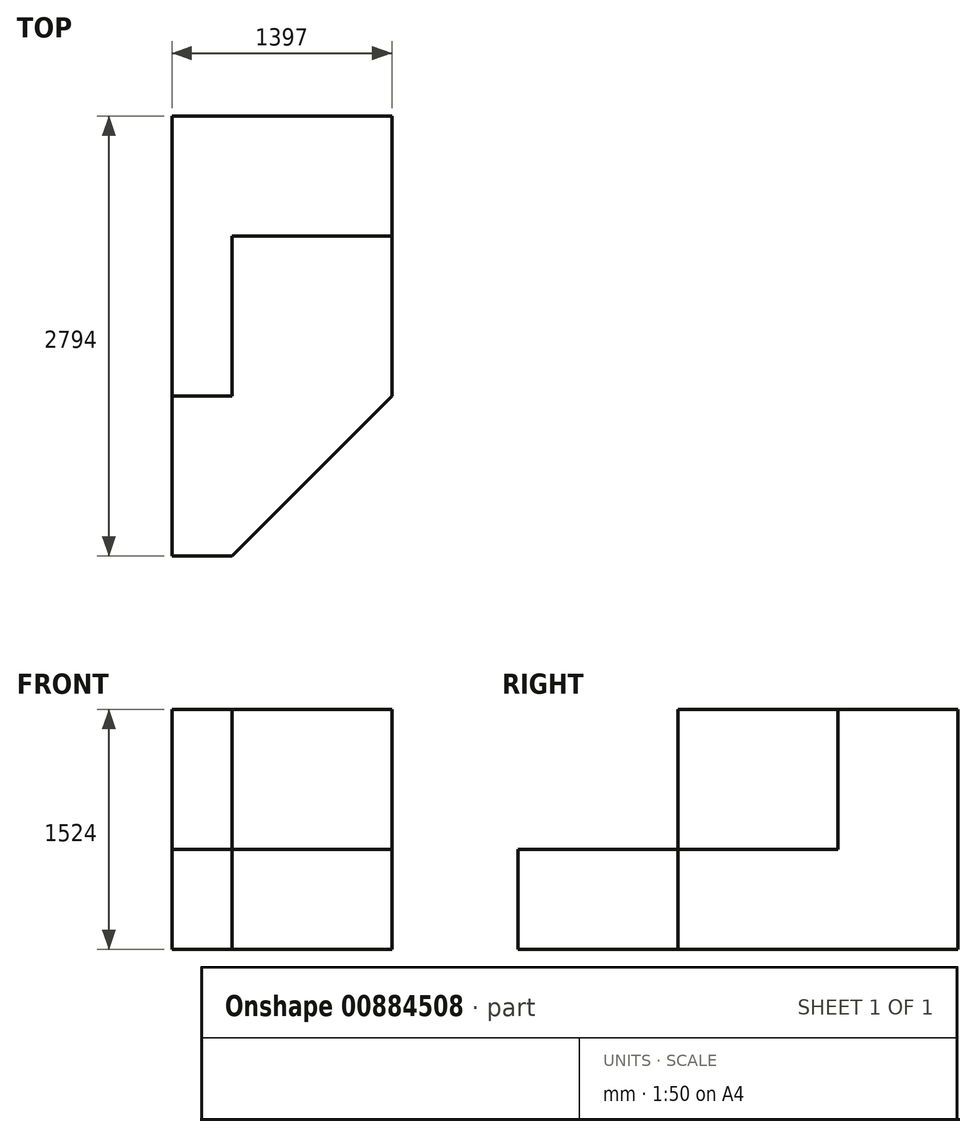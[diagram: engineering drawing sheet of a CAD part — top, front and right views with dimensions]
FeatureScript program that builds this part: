
annotation { "Feature Type Name" : "Feature", "Feature Type Description" : "" }
export const myFeature = defineFeature(function(context is Context, id is Id, definition is map)
    precondition{}
    {
        {
            var Q0;
            Q0=qCreatedBy(makeId("Top.planeOp"),FACE);
            var sketch = newSketch(context, id + "F0", { "sketchPlane" : qUnion([Q0])});
            skLineSegment(sketch, "E0.bottom", {"start": v(-1340.32, 2749.23) * mm, "end": v(56.68, 2749.23) * mm});
            skLineSegment(sketch, "E0.top", {"start": v(-1340.32, -44.77) * mm, "end": v(56.68, -44.77) * mm});
            skLineSegment(sketch, "E0.left", {"start": v(-1340.32, 2749.23) * mm, "end": v(-1340.32, -44.77) * mm});
            skLineSegment(sketch, "E0.right", {"start": v(56.68, 2749.23) * mm, "end": v(56.68, -44.77) * mm});
            skSolve(sketch);
        }
        {
            var Q0;
            Q0=makeQuery(id+"F0.imprint","IMPRINT",FACE,{"disambiguationData":[TD([[makeQuery(id+"F0.imprint","IMPRINT",EDGE,{"derivedFrom":sQuery(id+"F0.wireOp",EDGE,"E0.bottom")}),-1.0]])]});
            extrude(context, id + "F1", {"entities" : qUnion([Q0]), "depth" : 635 * mm, "offsetDistance" : 25.4 * mm});
        }
        {
            var Q0;
            Q0=makeQuery(id+"F1.opExtrude","CAP_FACE",FACE,{"disambiguationData":[OSD([sQuery(id+"F0.wireOp",EDGE,"E0.bottom"),sQuery(id+"F0.wireOp",EDGE,"E0.top"),sQuery(id+"F0.wireOp",EDGE,"E0.left"),sQuery(id+"F0.wireOp",EDGE,"E0.right")])],"isStart":false});
            var sketch = newSketch(context, id + "F2", { "sketchPlane" : qUnion([Q0])});
            skLineSegment(sketch, "E1", {"start": v(56.68, -44.77) * mm, "end": v(-959.32, -44.77) * mm});
            skLineSegment(sketch, "E2", {"start": v(56.68, -44.77) * mm, "end": v(56.68, 971.23) * mm});
            skLineSegment(sketch, "E3", {"start": v(56.68, 971.23) * mm, "end": v(-959.32, -44.77) * mm});
            skSolve(sketch);
        }
        {
            var Q0;
            Q0=makeQuery(id+"F2.imprint","IMPRINT",FACE,{"disambiguationData":[TD([[makeQuery(id+"F2.imprint","IMPRINT",EDGE,{"derivedFrom":sQuery(id+"F2.wireOp",EDGE,"E1")}),1.0]])]});
            extrude(context, id + "F3", {"entities" : qUnion([Q0]), "operationType" : NewBodyOperationType.REMOVE, "oppositeDirection" : true, "depth" : 660.4 * mm, "offsetDistance" : 25.4 * mm});
        }
        {
            var Q0;
            Q0=makeQuery(id+"F1.opExtrude","CAP_FACE",FACE,{"disambiguationData":[OSD([sQuery(id+"F0.wireOp",EDGE,"E0.bottom"),sQuery(id+"F0.wireOp",EDGE,"E0.top"),sQuery(id+"F0.wireOp",EDGE,"E0.left"),sQuery(id+"F0.wireOp",EDGE,"E0.right")])],"isStart":false});
            var sketch = newSketch(context, id + "F4", { "sketchPlane" : qUnion([Q0])});
            skLineSegment(sketch, "E4.bottom", {"start": v(-1340.32, 2749.23) * mm, "end": v(56.68, 2749.23) * mm});
            skLineSegment(sketch, "E4.top", {"start": v(-1340.32, 971.23) * mm, "end": v(56.68, 971.23) * mm});
            skLineSegment(sketch, "E4.left", {"start": v(-1340.32, 2749.23) * mm, "end": v(-1340.32, 971.23) * mm});
            skLineSegment(sketch, "E4.right", {"start": v(56.68, 2749.23) * mm, "end": v(56.68, 971.23) * mm});
            skSolve(sketch);
        }
        {
            var Q0;
            Q0=makeQuery(id+"F4.imprint","IMPRINT",FACE,{"disambiguationData":[TD([[makeQuery(id+"F4.imprint","IMPRINT",EDGE,{"derivedFrom":sQuery(id+"F4.wireOp",EDGE,"E4.bottom")}),-1.0]])]});
            extrude(context, id + "F5", {"entities" : qUnion([Q0]), "operationType" : NewBodyOperationType.ADD, "depth" : 889 * mm, "offsetDistance" : 25.4 * mm});
        }
        {
            var Q0;
            Q0=makeQuery(id+"F5.opExtrude","CAP_FACE",FACE,{"disambiguationData":[OSD([sQuery(id+"F4.wireOp",EDGE,"E4.bottom"),sQuery(id+"F4.wireOp",EDGE,"E4.top"),sQuery(id+"F4.wireOp",EDGE,"E4.left"),sQuery(id+"F4.wireOp",EDGE,"E4.right")])],"isStart":false});
            var sketch = newSketch(context, id + "F6", { "sketchPlane" : qUnion([Q0])});
            skLineSegment(sketch, "E5.bottom", {"start": v(56.68, 971.23) * mm, "end": v(-959.32, 971.23) * mm});
            skLineSegment(sketch, "E5.top", {"start": v(56.68, 1987.23) * mm, "end": v(-959.32, 1987.23) * mm});
            skLineSegment(sketch, "E5.left", {"start": v(56.68, 971.23) * mm, "end": v(56.68, 1987.23) * mm});
            skLineSegment(sketch, "E5.right", {"start": v(-959.32, 971.23) * mm, "end": v(-959.32, 1987.23) * mm});
            skSolve(sketch);
        }
        {
            var Q0;
            Q0=makeQuery(id+"F6.imprint","IMPRINT",FACE,{"disambiguationData":[TD([[makeQuery(id+"F6.imprint","IMPRINT",EDGE,{"derivedFrom":sQuery(id+"F6.wireOp",EDGE,"E5.bottom")}),1.0]])]});
            extrude(context, id + "F7", {"entities" : qUnion([Q0]), "operationType" : NewBodyOperationType.REMOVE, "oppositeDirection" : true, "depth" : 889 * mm, "offsetDistance" : 25.4 * mm});
        }
    });
